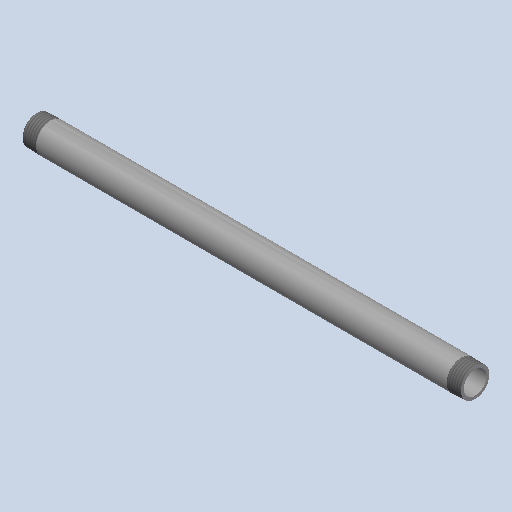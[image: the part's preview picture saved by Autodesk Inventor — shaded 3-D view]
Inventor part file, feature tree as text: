
AUTODESK INVENTOR PART (.ipt)
format: ipt  version: 2025 (Build 290162000, 162)  size: 178,176 bytes
history: native  units: mm (DEFAULTED — no unit token found)
features: other x8, revolve x1
ambient origin geometry x8: Origin, YZ Plane, XZ Plane, XY Plane, X Axis, Y Axis, Z Axis, Center Point
bodies: Solid1 (feature_tree)
feature tree (9):
  revolve  "Revolution1"  [1 undecoded]
  other  "Work Axis1"
  other  "Work Point5"
  other  "Work Axis2"
  other  "Work Point6"
  other  "Work Axis3"
  other  "Work Axis4"
  other  "Work Point7"
  other  "Work Point8"
note: 1 required parameter value undecoded (feature->parameter linkage not recoverable at this tier; creation-order binding heuristic only, values carry confidence <= 0.55)
